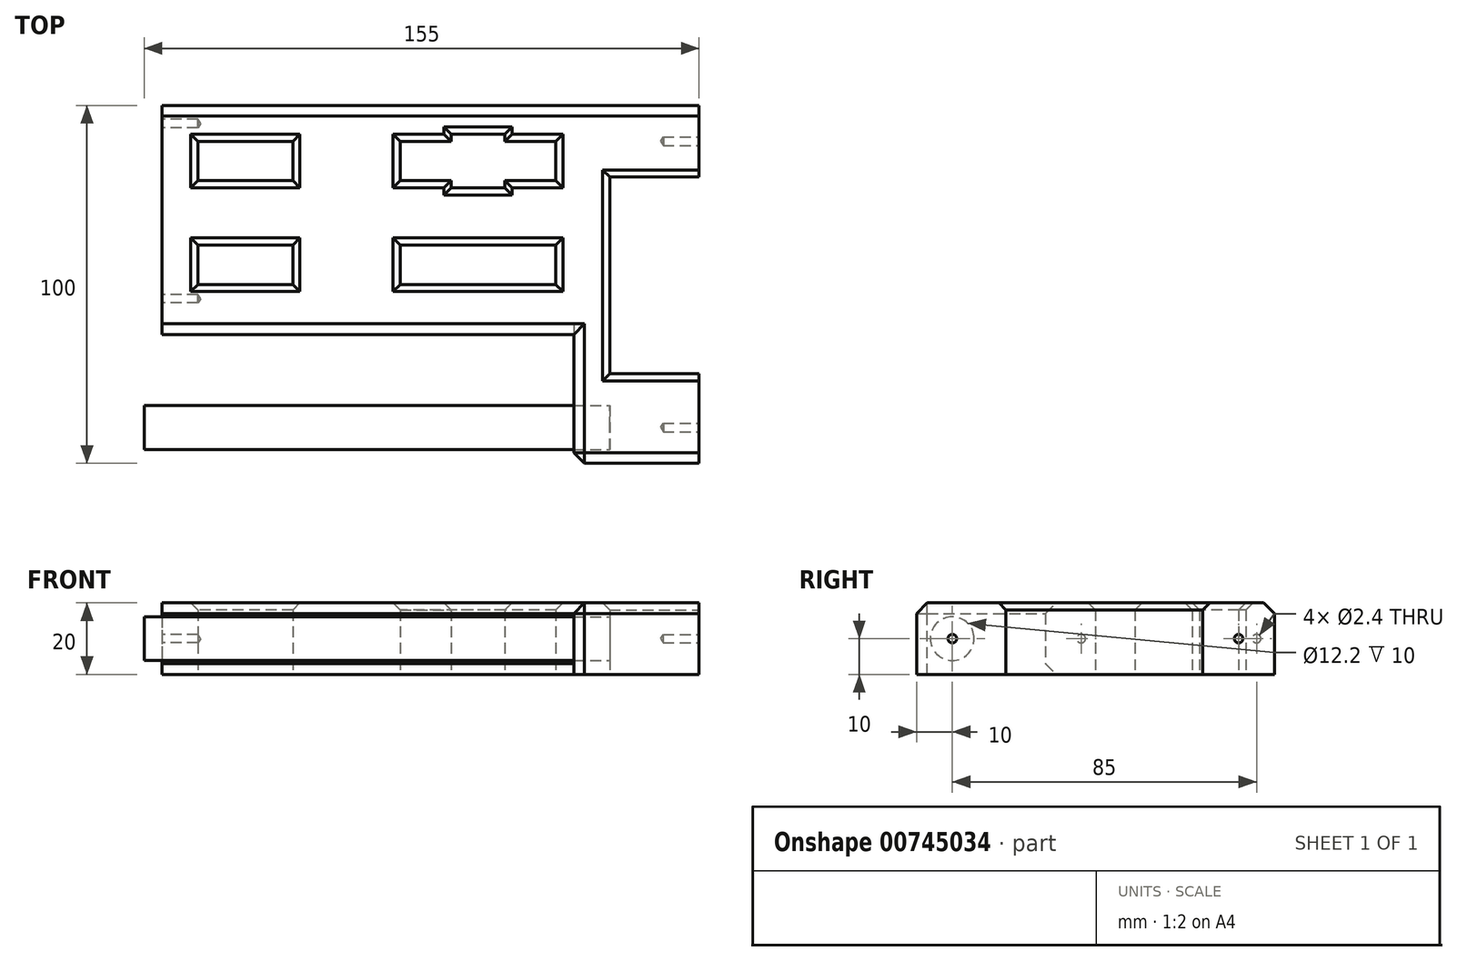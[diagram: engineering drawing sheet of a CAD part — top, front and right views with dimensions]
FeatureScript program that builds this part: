
annotation { "Feature Type Name" : "Feature", "Feature Type Description" : "" }
export const myFeature = defineFeature(function(context is Context, id is Id, definition is map)
    precondition{}
    {
        {
            var Q0;
            Q0=qCreatedBy(makeId("Top.planeOp"),FACE);
            var sketch = newSketch(context, id + "F0", { "sketchPlane" : qUnion([Q0])});
            skLineSegment(sketch, "E0.bottom", {"start": v(75, -50) * mm, "end": v(40, -50) * mm});
            skLineSegment(sketch, "E0.top", {"start": v(75, 50) * mm, "end": v(-75, 50) * mm});
            skLineSegment(sketch, "E0.left", {"start": v(75, -50) * mm, "end": v(75, -25) * mm});
            skLineSegment(sketch, "E0.right", {"start": v(-75, -14) * mm, "end": v(-75, 50) * mm});
            skPoint(sketch, "E0.middle", {"position": v(0, 0) * mm});
            skLineSegment(sketch, "E1.top", {"start": v(-75, -14) * mm, "end": v(40, -14) * mm});
            skLineSegment(sketch, "E1.right", {"start": v(40, -50) * mm, "end": v(40, -14) * mm});
            skPoint(sketch, "E2.orphan", {"position": v(-75, -50) * mm});
            skLineSegment(sketch, "E3", {"start": v(75, -25) * mm, "end": v(50, -25) * mm});
            skLineSegment(sketch, "E4", {"start": v(50, -25) * mm, "end": v(50, 30) * mm});
            skLineSegment(sketch, "E5", {"start": v(50, 30) * mm, "end": v(75, 30) * mm});
            skLineSegment(sketch, "E6.trimOffspring", {"start": v(75, 30) * mm, "end": v(75, 50) * mm});
            skLineSegment(sketch, "E7.bottom", {"start": v(-65, 40) * mm, "end": v(-38.5, 40) * mm});
            skLineSegment(sketch, "E7.top", {"start": v(-65, 29) * mm, "end": v(-38.5, 29) * mm});
            skLineSegment(sketch, "E7.left", {"start": v(-65, 40) * mm, "end": v(-65, 29) * mm});
            skLineSegment(sketch, "E7.right", {"start": v(-38.5, 40) * mm, "end": v(-38.5, 29) * mm});
            skLineSegment(sketch, "E8.bottom", {"start": v(-8.5, 40) * mm, "end": v(5.75, 40) * mm});
            skLineSegment(sketch, "E8.top", {"start": v(-8.5, 29) * mm, "end": v(5.75, 29) * mm});
            skLineSegment(sketch, "E8.left", {"start": v(-8.5, 40) * mm, "end": v(-8.5, 29) * mm});
            skLineSegment(sketch, "E8.right", {"start": v(35, 40) * mm, "end": v(35, 29) * mm});
            skLineSegment(sketch, "E9.bottom", {"start": v(-8.5, 11) * mm, "end": v(35, 11) * mm});
            skLineSegment(sketch, "E9.top", {"start": v(-8.5, 0) * mm, "end": v(35, 0) * mm});
            skLineSegment(sketch, "E9.left", {"start": v(-8.5, 11) * mm, "end": v(-8.5, 0) * mm});
            skLineSegment(sketch, "E9.right", {"start": v(35, 11) * mm, "end": v(35, 0) * mm});
            skLineSegment(sketch, "E10.bottom", {"start": v(-65, 11) * mm, "end": v(-38.5, 11) * mm});
            skLineSegment(sketch, "E10.top", {"start": v(-65, 0) * mm, "end": v(-38.5, 0) * mm});
            skLineSegment(sketch, "E10.left", {"start": v(-65, 11) * mm, "end": v(-65, 0) * mm});
            skLineSegment(sketch, "E10.right", {"start": v(-38.5, 11) * mm, "end": v(-38.5, 0) * mm});
            skPoint(sketch, "E11", {"position": v(13.25, 34.5) * mm});
            skPoint(sketch, "E11.positionSnap0", {"position": v(-8.5, 34.5) * mm});
            skPoint(sketch, "E11.positionSnap1", {"position": v(13.25, 40) * mm});
            skLineSegment(sketch, "E12.bottom", {"start": v(20.75, 27) * mm, "end": v(5.75, 27) * mm});
            skLineSegment(sketch, "E12.top", {"start": v(20.75, 42) * mm, "end": v(5.75, 42) * mm});
            skLineSegment(sketch, "E12.left", {"start": v(20.75, 27) * mm, "end": v(20.75, 29) * mm});
            skLineSegment(sketch, "E12.right", {"start": v(5.75, 27) * mm, "end": v(5.75, 29) * mm});
            skLineSegment(sketch, "E13.trimOffspring", {"start": v(5.75, 40) * mm, "end": v(5.75, 42) * mm});
            skLineSegment(sketch, "E14.trimOffspring", {"start": v(20.75, 29) * mm, "end": v(35, 29) * mm});
            skLineSegment(sketch, "E15.trimOffspring", {"start": v(20.75, 40) * mm, "end": v(20.75, 42) * mm});
            skLineSegment(sketch, "E16.trimOffspring", {"start": v(20.75, 40) * mm, "end": v(35, 40) * mm});
            skSolve(sketch);
        }
        {
            var Q0;
            Q0=makeQuery(id+"F0.imprint","IMPRINT",FACE,{"disambiguationData":[TD([[makeQuery(id+"F0.imprint","IMPRINT",EDGE,{"derivedFrom":sQuery(id+"F0.wireOp",EDGE,"E0.bottom")}),-1.0]])]});
            extrude(context, id + "F1", {"entities" : qUnion([Q0]), "depth" : 20 * mm, "offsetDistance" : 25 * mm});
        }
        {
            var Q0;
            Q0=makeQuery(id+"F1.opExtrude","CAP_EDGE",EDGE,{"disambiguationData":[OSD([sQuery(id+"F0.wireOp",EDGE,"E10.bottom")])],"isStart":false});
            var Q1;
            Q1=makeQuery(id+"F1.opExtrude","CAP_EDGE",EDGE,{"disambiguationData":[OSD([sQuery(id+"F0.wireOp",EDGE,"E10.left")])],"isStart":false});
            var Q2;
            Q2=makeQuery(id+"F1.opExtrude","CAP_EDGE",EDGE,{"disambiguationData":[OSD([sQuery(id+"F0.wireOp",EDGE,"E10.top")])],"isStart":false});
            var Q3;
            Q3=makeQuery(id+"F1.opExtrude","CAP_EDGE",EDGE,{"disambiguationData":[OSD([sQuery(id+"F0.wireOp",EDGE,"E10.right")])],"isStart":false});
            var Q4;
            Q4=makeQuery(id+"F1.opExtrude","CAP_EDGE",EDGE,{"disambiguationData":[OSD([sQuery(id+"F0.wireOp",EDGE,"E7.right")])],"isStart":false});
            var Q5;
            Q5=makeQuery(id+"F1.opExtrude","CAP_EDGE",EDGE,{"disambiguationData":[OSD([sQuery(id+"F0.wireOp",EDGE,"E7.bottom")])],"isStart":false});
            var Q6;
            Q6=makeQuery(id+"F1.opExtrude","CAP_EDGE",EDGE,{"disambiguationData":[OSD([sQuery(id+"F0.wireOp",EDGE,"E7.top")])],"isStart":false});
            var Q7;
            Q7=makeQuery(id+"F1.opExtrude","CAP_EDGE",EDGE,{"disambiguationData":[OSD([sQuery(id+"F0.wireOp",EDGE,"E7.left")])],"isStart":false});
            var Q8;
            Q8=makeQuery(id+"F1.opExtrude","CAP_EDGE",EDGE,{"disambiguationData":[OSD([sQuery(id+"F0.wireOp",EDGE,"E9.bottom")])],"isStart":false});
            var Q9;
            Q9=makeQuery(id+"F1.opExtrude","CAP_EDGE",EDGE,{"disambiguationData":[OSD([sQuery(id+"F0.wireOp",EDGE,"E9.left")])],"isStart":false});
            var Q10;
            Q10=makeQuery(id+"F1.opExtrude","CAP_EDGE",EDGE,{"disambiguationData":[OSD([sQuery(id+"F0.wireOp",EDGE,"E9.top")])],"isStart":false});
            var Q11;
            Q11=makeQuery(id+"F1.opExtrude","CAP_EDGE",EDGE,{"disambiguationData":[OSD([sQuery(id+"F0.wireOp",EDGE,"E9.right")])],"isStart":false});
            var Q12;
            Q12=makeQuery(id+"F1.opExtrude","CAP_EDGE",EDGE,{"disambiguationData":[OSD([sQuery(id+"F0.wireOp",EDGE,"E5")])],"isStart":false});
            var Q13;
            Q13=makeQuery(id+"F1.opExtrude","CAP_EDGE",EDGE,{"disambiguationData":[OSD([sQuery(id+"F0.wireOp",EDGE,"E4")])],"isStart":false});
            var Q14;
            Q14=makeQuery(id+"F1.opExtrude","CAP_EDGE",EDGE,{"disambiguationData":[OSD([sQuery(id+"F0.wireOp",EDGE,"E3")])],"isStart":false});
            var Q15;
            Q15=makeQuery(id+"F1.opExtrude","CAP_EDGE",EDGE,{"disambiguationData":[OSD([sQuery(id+"F0.wireOp",EDGE,"E12.top")])],"isStart":false});
            var Q16;
            Q16=makeQuery(id+"F1.opExtrude","CAP_EDGE",EDGE,{"disambiguationData":[OSD([sQuery(id+"F0.wireOp",EDGE,"E13.trimOffspring")])],"isStart":false});
            var Q17;
            Q17=makeQuery(id+"F1.opExtrude","CAP_EDGE",EDGE,{"disambiguationData":[OSD([sQuery(id+"F0.wireOp",EDGE,"E16.trimOffspring")])],"isStart":false});
            var Q18;
            Q18=makeQuery(id+"F1.opExtrude","CAP_EDGE",EDGE,{"disambiguationData":[OSD([sQuery(id+"F0.wireOp",EDGE,"E15.trimOffspring")])],"isStart":false});
            var Q19;
            Q19=makeQuery(id+"F1.opExtrude","CAP_EDGE",EDGE,{"disambiguationData":[OSD([sQuery(id+"F0.wireOp",EDGE,"E12.right")])],"isStart":false});
            var Q20;
            Q20=makeQuery(id+"F1.opExtrude","CAP_EDGE",EDGE,{"disambiguationData":[OSD([sQuery(id+"F0.wireOp",EDGE,"E12.bottom")])],"isStart":false});
            var Q21;
            Q21=makeQuery(id+"F1.opExtrude","CAP_EDGE",EDGE,{"disambiguationData":[OSD([sQuery(id+"F0.wireOp",EDGE,"E12.left")])],"isStart":false});
            var Q22;
            Q22=makeQuery(id+"F1.opExtrude","CAP_EDGE",EDGE,{"disambiguationData":[OSD([sQuery(id+"F0.wireOp",EDGE,"E14.trimOffspring")])],"isStart":false});
            var Q23;
            Q23=makeQuery(id+"F1.opExtrude","CAP_EDGE",EDGE,{"disambiguationData":[OSD([sQuery(id+"F0.wireOp",EDGE,"E8.left")])],"isStart":false});
            var Q24;
            Q24=makeQuery(id+"F1.opExtrude","CAP_EDGE",EDGE,{"disambiguationData":[OSD([sQuery(id+"F0.wireOp",EDGE,"E8.bottom")])],"isStart":false});
            var Q25;
            Q25=makeQuery(id+"F1.opExtrude","CAP_EDGE",EDGE,{"disambiguationData":[OSD([sQuery(id+"F0.wireOp",EDGE,"E8.top")])],"isStart":false});
            var Q26;
            Q26=makeQuery(id+"F1.opExtrude","CAP_EDGE",EDGE,{"disambiguationData":[OSD([sQuery(id+"F0.wireOp",EDGE,"E8.right")])],"isStart":false});
            chamfer(context, id + "F2", {"entities" : qUnion([Q0, Q1, Q2, Q3, Q4, Q5, Q6, Q7, Q8, Q9, Q10, Q11, Q12, Q13, Q14, Q15, Q16, Q17, Q18, Q19, Q20, Q21, Q22, Q23, Q24, Q25, Q26]), "width" : 2 * mm, "tangentPropagation" : true});
        }
        {
            var Q0;
            Q0=makeQuery(id+"F1.opExtrude","SWEPT_FACE",FACE,{"disambiguationData":[OSD([sQuery(id+"F0.wireOp",EDGE,"E1.right")])]});
            var sketch = newSketch(context, id + "F3", { "sketchPlane" : qUnion([Q0])});
            skCircle(sketch, "E17", {"center": v(40, 10) * mm, "radius": 6.1 * mm});
            skSolve(sketch);
        }
        {
            var Q0;
            Q0=makeQuery(id+"F3.imprint","IMPRINT",FACE,{"disambiguationData":[TD([[makeQuery(id+"F3.imprint","IMPRINT",EDGE,{"derivedFrom":sQuery(id+"F3.wireOp",EDGE,"E17")}),1.0]])]});
            extrude(context, id + "F4", {"entities" : qUnion([Q0]), "operationType" : NewBodyOperationType.REMOVE, "oppositeDirection" : true, "depth" : 10 * mm, "offsetDistance" : 25 * mm});
        }
        {
            var Q0;
            Q0=makeQuery(id+"F4.boolean.opBoolean","COPY",FACE,{"derivedFrom":makeQuery(id+"F4.opExtrude","CAP_FACE",FACE,{"disambiguationData":[OSD([sQuery(id+"F3.wireOp",EDGE,"E17")])],"isStart":false})});
            extrude(context, id + "F5", {"entities" : qUnion([Q0]), "depth" : 130 * mm, "offsetDistance" : 25 * mm});
        }
        {
            var Q0;
            Q0=makeQuery(id+"F1.opExtrude","SWEPT_FACE",FACE,{"disambiguationData":[OSD([sQuery(id+"F0.wireOp",EDGE,"E0.left")])]});
            var sketch = newSketch(context, id + "F6", { "sketchPlane" : qUnion([Q0])});
            skPoint(sketch, "E18", {"position": v(-40, 10) * mm});
            skPoint(sketch, "E19", {"position": v(40, 10) * mm});
            skSolve(sketch);
        }
        {
            var Q0;
            Q0=makeQuery(id+"F1.opExtrude","SWEPT_FACE",FACE,{"disambiguationData":[OSD([sQuery(id+"F0.wireOp",EDGE,"E0.right")])]});
            var sketch = newSketch(context, id + "F7", { "sketchPlane" : qUnion([Q0])});
            skPoint(sketch, "E20", {"position": v(-45, 10) * mm});
            skPoint(sketch, "E21", {"position": v(4, 10) * mm});
            skSolve(sketch);
        }
        {
            var Q0;
            Q0=sQuery(id+"F6.wireOp",VERTEX,"E18");
            var Q1;
            Q1=sQuery(id+"F6.wireOp",VERTEX,"E19");
            var Q2;
            Q2=sQuery(id+"F7.wireOp",VERTEX,"E21");
            var Q3;
            Q3=sQuery(id+"F7.wireOp",VERTEX,"E20");
            var Q4;
            Q4=makeQuery(id+"F1.opExtrude","SWEPT_BODY",BODY,{"disambiguationData":[OSD([sQuery(id+"F0.wireOp",EDGE,"E0.bottom"),sQuery(id+"F0.wireOp",EDGE,"E0.top"),sQuery(id+"F0.wireOp",EDGE,"E0.left"),sQuery(id+"F0.wireOp",EDGE,"E0.right"),sQuery(id+"F0.wireOp",EDGE,"E1.top"),sQuery(id+"F0.wireOp",EDGE,"E1.right"),sQuery(id+"F0.wireOp",EDGE,"E3"),sQuery(id+"F0.wireOp",EDGE,"E4"),sQuery(id+"F0.wireOp",EDGE,"E5"),sQuery(id+"F0.wireOp",EDGE,"E6.trimOffspring"),sQuery(id+"F0.wireOp",EDGE,"E7.bottom"),sQuery(id+"F0.wireOp",EDGE,"E7.top"),sQuery(id+"F0.wireOp",EDGE,"E7.left"),sQuery(id+"F0.wireOp",EDGE,"E7.right"),sQuery(id+"F0.wireOp",EDGE,"E8.bottom"),sQuery(id+"F0.wireOp",EDGE,"E8.top"),sQuery(id+"F0.wireOp",EDGE,"E8.left"),sQuery(id+"F0.wireOp",EDGE,"E8.right"),sQuery(id+"F0.wireOp",EDGE,"E9.bottom"),sQuery(id+"F0.wireOp",EDGE,"E9.top"),sQuery(id+"F0.wireOp",EDGE,"E9.left"),sQuery(id+"F0.wireOp",EDGE,"E9.right")])]});
            hole(context, id + "F8", {"style" : HoleStyle.SIMPLE, "endStyle" : HoleEndStyle.BLIND, "holeDiameter" : 2.4 * mm, "majorDiameter" : 5 * mm, "holeDepth" : 10 * mm, "isTappedThrough" : true, "tappedDepth" : 6 * mm, "tapClearance" : 3, "locations" : qUnion([Q0, Q1, Q2, Q3]), "scope" : qUnion([Q4])});
        }
        {
            var Q0;
            Q0=makeQuery(id+"F1.opExtrude","CAP_EDGE",EDGE,{"disambiguationData":[OSD([sQuery(id+"F0.wireOp",EDGE,"E0.top")])],"isStart":false});
            var Q1;
            Q1=makeQuery(id+"F1.opExtrude","CAP_EDGE",EDGE,{"disambiguationData":[OSD([sQuery(id+"F0.wireOp",EDGE,"E1.right")])],"isStart":false});
            var Q2;
            Q2=makeQuery(id+"F1.opExtrude","SWEPT_EDGE",EDGE,{"disambiguationData":[OSD([sQuery(id+"F0.wireOp",EDGE,"E0.bottom"),sQuery(id+"F0.wireOp",EDGE,"E1.right")])]});
            var Q3;
            Q3=makeQuery(id+"F1.opExtrude","CAP_EDGE",EDGE,{"disambiguationData":[OSD([sQuery(id+"F0.wireOp",EDGE,"E0.bottom")])],"isStart":false});
            var Q4;
            Q4=makeQuery(id+"F1.opExtrude","CAP_EDGE",EDGE,{"disambiguationData":[OSD([sQuery(id+"F0.wireOp",EDGE,"E1.top")])],"isStart":false});
            var Q5;
            Q5=makeQuery(id+"F1.opExtrude","CAP_EDGE",EDGE,{"disambiguationData":[OSD([sQuery(id+"F0.wireOp",EDGE,"E1.top")])],"isStart":true});
            chamfer(context, id + "F9", {"entities" : qUnion([Q0, Q1, Q2, Q3, Q4, Q5]), "width" : 3 * mm, "tangentPropagation" : true});
        }
    });
